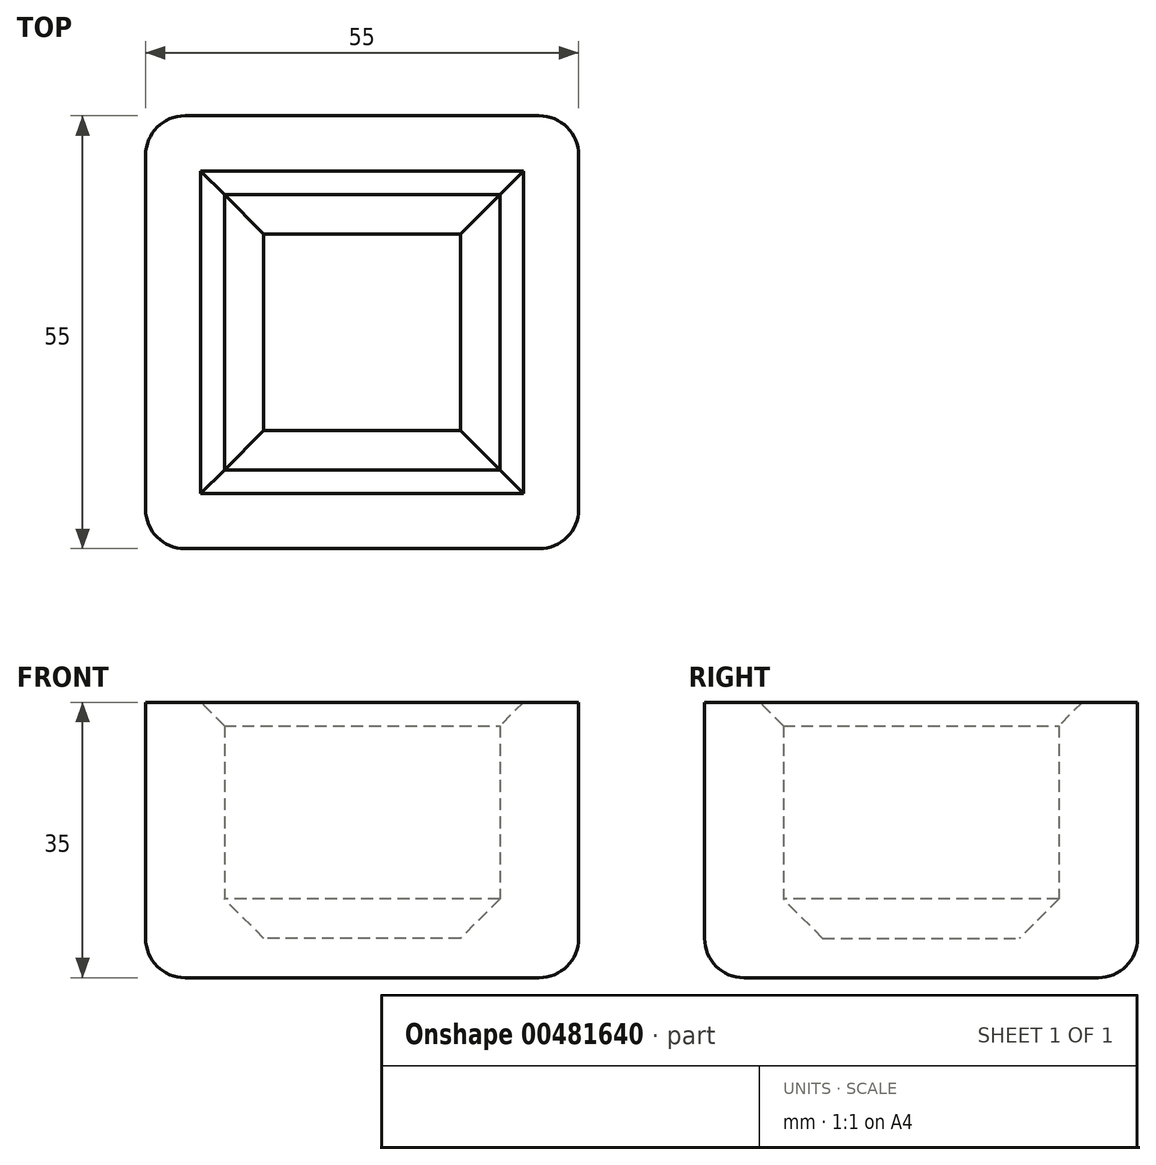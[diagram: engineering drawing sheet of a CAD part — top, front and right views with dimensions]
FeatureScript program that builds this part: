
annotation { "Feature Type Name" : "Feature", "Feature Type Description" : "" }
export const myFeature = defineFeature(function(context is Context, id is Id, definition is map)
    precondition{}
    {
        {
            var Q0;
            Q0=qCreatedBy(makeId("Top.planeOp"),FACE);
            var sketch = newSketch(context, id + "F0", { "sketchPlane" : qUnion([Q0])});
            skLineSegment(sketch, "E0.bottom", {"start": v(17.5, -17.5) * mm, "end": v(-17.5, -17.5) * mm});
            skLineSegment(sketch, "E0.top", {"start": v(17.5, 17.5) * mm, "end": v(-17.5, 17.5) * mm});
            skLineSegment(sketch, "E0.left", {"start": v(17.5, -17.5) * mm, "end": v(17.5, 17.5) * mm});
            skLineSegment(sketch, "E0.right", {"start": v(-17.5, -17.5) * mm, "end": v(-17.5, 17.5) * mm});
            skPoint(sketch, "E0.middle", {"position": v(0, 0) * mm});
            skLineSegment(sketch, "E1.0", {"start": v(27.5, -27.5) * mm, "end": v(-27.5, -27.5) * mm});
            skLineSegment(sketch, "E1.1", {"start": v(27.5, -27.5) * mm, "end": v(27.5, 27.5) * mm});
            skLineSegment(sketch, "E1.2", {"start": v(27.5, 27.5) * mm, "end": v(-27.5, 27.5) * mm});
            skLineSegment(sketch, "E1.3", {"start": v(-27.5, -27.5) * mm, "end": v(-27.5, 27.5) * mm});
            skSolve(sketch);
        }
        {
            var Q0;
            Q0 = qSketchRegion(id + "F0", true);
            var Q1;
            Q1=makeQuery(id+"F0.imprint","IMPRINT",FACE,{"disambiguationData":[TD([[makeQuery(id+"F0.imprint","IMPRINT",EDGE,{"derivedFrom":sQuery(id+"F0.wireOp",EDGE,"E0.bottom")}),-1.0]])]});
            extrude(context, id + "F1", {"entities" : qUnion([Q0, Q1]), "oppositeDirection" : true, "depth" : 5 * mm, "offsetDistance" : 25 * mm});
        }
        {
            var Q0;
            Q0=makeQuery(id+"F0.imprint","IMPRINT",FACE,{"disambiguationData":[TD([[makeQuery(id+"F0.imprint","IMPRINT",EDGE,{"derivedFrom":sQuery(id+"F0.wireOp",EDGE,"E0.bottom")}),1.0]])]});
            extrude(context, id + "F2", {"entities" : qUnion([Q0]), "operationType" : NewBodyOperationType.ADD, "depth" : 30 * mm, "offsetDistance" : 25 * mm});
        }
        {
            var Q0;
            Q0=makeQuery(id+"F1.opExtrude","CAP_FACE",FACE,{"disambiguationData":[OSD([sQuery(id+"F0.wireOp",EDGE,"E1.0"),sQuery(id+"F0.wireOp",EDGE,"E1.1"),sQuery(id+"F0.wireOp",EDGE,"E1.2"),sQuery(id+"F0.wireOp",EDGE,"E1.3")])],"isStart":false});
            var Q1;
            {var subQ0=sQuery(id+"F0.wireOp",EDGE,"E1.2");var subQ1=sQuery(id+"F0.wireOp",EDGE,"E1.1");Q1=makeQuery(id+"F2.boolean.opBoolean","MERGE",EDGE,{"derivedFrom":[makeQuery(id+"F1.opExtrude","SWEPT_EDGE",EDGE,{"disambiguationData":[OSD([subQ1,subQ0])]}),makeQuery(id+"F2.opExtrude","SWEPT_EDGE",EDGE,{"disambiguationData":[OSD([subQ1,subQ0])]})]});}
            var Q2;
            {var subQ0=sQuery(id+"F0.wireOp",EDGE,"E1.3");var subQ1=sQuery(id+"F0.wireOp",EDGE,"E1.2");Q2=makeQuery(id+"F2.boolean.opBoolean","MERGE",EDGE,{"derivedFrom":[makeQuery(id+"F1.opExtrude","SWEPT_EDGE",EDGE,{"disambiguationData":[OSD([subQ1,subQ0])]}),makeQuery(id+"F2.opExtrude","SWEPT_EDGE",EDGE,{"disambiguationData":[OSD([subQ1,subQ0])]})]});}
            var Q3;
            {var subQ0=sQuery(id+"F0.wireOp",EDGE,"E1.3");var subQ1=sQuery(id+"F0.wireOp",EDGE,"E1.0");Q3=makeQuery(id+"F2.boolean.opBoolean","MERGE",EDGE,{"derivedFrom":[makeQuery(id+"F1.opExtrude","SWEPT_EDGE",EDGE,{"disambiguationData":[OSD([subQ1,subQ0])]}),makeQuery(id+"F2.opExtrude","SWEPT_EDGE",EDGE,{"disambiguationData":[OSD([subQ1,subQ0])]})]});}
            var Q4;
            {var subQ0=sQuery(id+"F0.wireOp",EDGE,"E1.1");var subQ1=sQuery(id+"F0.wireOp",EDGE,"E1.0");Q4=makeQuery(id+"F2.boolean.opBoolean","MERGE",EDGE,{"derivedFrom":[makeQuery(id+"F1.opExtrude","SWEPT_EDGE",EDGE,{"disambiguationData":[OSD([subQ1,subQ0])]}),makeQuery(id+"F2.opExtrude","SWEPT_EDGE",EDGE,{"disambiguationData":[OSD([subQ1,subQ0])]})]});}
            fillet(context, id + "F3", {"entities" : qUnion([Q0, Q1, Q2, Q3, Q4]), "tangentPropagation" : true, "radius" : 5 * mm, "defaultsChanged" : false, "vertexSettings" : [], "allowEdgeOverflow" : false});
        }
        {
            var Q0;
            Q0=makeQuery(id+"F2.opExtrude","CAP_EDGE",EDGE,{"disambiguationData":[OSD([sQuery(id+"F0.wireOp",EDGE,"E0.right")])],"isStart":false});
            var Q1;
            Q1=makeQuery(id+"F2.opExtrude","CAP_EDGE",EDGE,{"disambiguationData":[OSD([sQuery(id+"F0.wireOp",EDGE,"E0.bottom")])],"isStart":false});
            var Q2;
            Q2=makeQuery(id+"F2.opExtrude","CAP_EDGE",EDGE,{"disambiguationData":[OSD([sQuery(id+"F0.wireOp",EDGE,"E0.left")])],"isStart":false});
            var Q3;
            Q3=makeQuery(id+"F2.opExtrude","CAP_EDGE",EDGE,{"disambiguationData":[OSD([sQuery(id+"F0.wireOp",EDGE,"E0.top")])],"isStart":false});
            chamfer(context, id + "F4", {"entities" : qUnion([Q0, Q1, Q2, Q3]), "width" : 3 * mm, "tangentPropagation" : true});
        }
        {
            var Q0;
            Q0=makeQuery(id+"F1.opExtrude","CAP_FACE",FACE,{"disambiguationData":[OSD([sQuery(id+"F0.wireOp",EDGE,"E1.0"),sQuery(id+"F0.wireOp",EDGE,"E1.1"),sQuery(id+"F0.wireOp",EDGE,"E1.2"),sQuery(id+"F0.wireOp",EDGE,"E1.3")])],"isStart":true});
            chamfer(context, id + "F5", {"entities" : qUnion([Q0]), "width" : 5 * mm, "tangentPropagation" : true});
        }
    });
